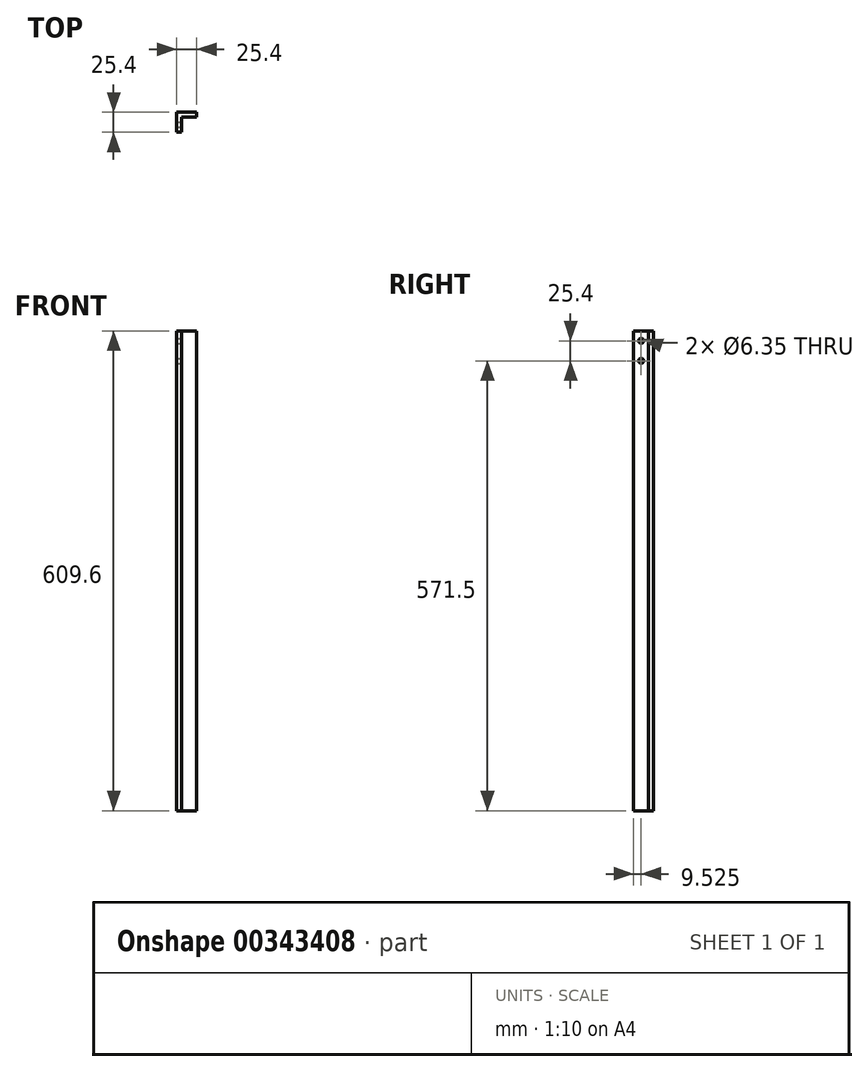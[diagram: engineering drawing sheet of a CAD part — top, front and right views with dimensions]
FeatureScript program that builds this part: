
annotation { "Feature Type Name" : "Feature", "Feature Type Description" : "" }
export const myFeature = defineFeature(function(context is Context, id is Id, definition is map)
    precondition{}
    {
        {
            var Q0;
            Q0=qCreatedBy(makeId("Top.planeOp"),FACE);
            var sketch = newSketch(context, id + "F0", { "sketchPlane" : qUnion([Q0])});
            skLineSegment(sketch, "E0", {"start": v(0, 0) * mm, "end": v(0, 25.4) * mm});
            skLineSegment(sketch, "E1", {"start": v(0, 25.4) * mm, "end": v(25.4, 25.4) * mm});
            skLineSegment(sketch, "E2", {"start": v(25.4, 25.4) * mm, "end": v(25.4, 19.05) * mm});
            skLineSegment(sketch, "E3", {"start": v(25.4, 19.05) * mm, "end": v(6.35, 19.05) * mm});
            skLineSegment(sketch, "E4", {"start": v(6.35, 19.05) * mm, "end": v(6.35, 0) * mm});
            skLineSegment(sketch, "E5", {"start": v(6.35, 0) * mm, "end": v(0, 0) * mm});
            skSolve(sketch);
        }
        {
            var Q0;
            Q0=makeQuery(id+"F0.imprint","IMPRINT",FACE,{"disambiguationData":[TD([[makeQuery(id+"F0.imprint","IMPRINT",EDGE,{"derivedFrom":sQuery(id+"F0.wireOp",EDGE,"E0")}),-1.0]])]});
            extrude(context, id + "F1", {"entities" : qUnion([Q0]), "depth" : 609.6 * mm});
        }
        {
            var Q0;
            Q0=makeQuery(id+"F1.opExtrude","SWEPT_FACE",FACE,{"disambiguationData":[OSD([sQuery(id+"F0.wireOp",EDGE,"E4")])]});
            var sketch = newSketch(context, id + "F2", { "sketchPlane" : qUnion([Q0])});
            skCircle(sketch, "E6", {"center": v(9.53, 596.9) * mm, "radius": 3.18 * mm});
            skLineSegment(sketch, "E7", {"start": v(9.53, 609.6) * mm, "end": v(9.53, 259.1) * mm, "construction": true});
            skCircle(sketch, "E8", {"center": v(9.53, 571.5) * mm, "radius": 3.18 * mm});
            skSolve(sketch);
        }
        {
            var Q0;
            Q0=makeQuery(id+"F2.imprint","IMPRINT",FACE,{"disambiguationData":[TD([[makeQuery(id+"F2.imprint","IMPRINT",EDGE,{"derivedFrom":sQuery(id+"F2.wireOp",EDGE,"E6")}),1.0]])]});
            var Q1;
            Q1=makeQuery(id+"F2.imprint","IMPRINT",FACE,{"disambiguationData":[TD([[makeQuery(id+"F2.imprint","IMPRINT",EDGE,{"derivedFrom":sQuery(id+"F2.wireOp",EDGE,"E8")}),1.0]])]});
            extrude(context, id + "F3", {"entities" : qUnion([Q0, Q1]), "operationType" : NewBodyOperationType.REMOVE, "oppositeDirection" : true, "depth" : 25.4 * mm});
        }
    });
